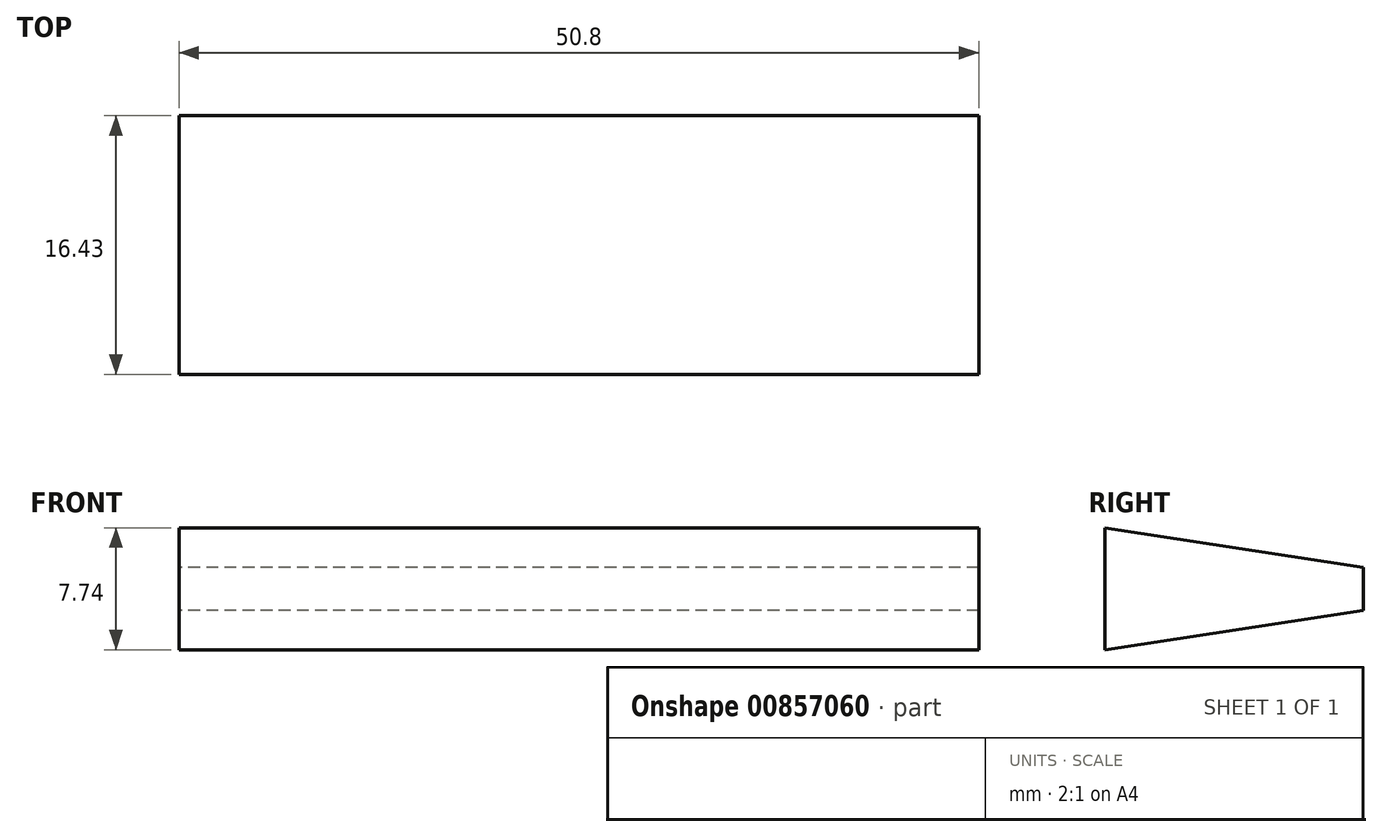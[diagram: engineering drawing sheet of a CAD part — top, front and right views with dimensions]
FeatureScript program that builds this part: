
annotation { "Feature Type Name" : "Feature", "Feature Type Description" : "" }
export const myFeature = defineFeature(function(context is Context, id is Id, definition is map)
    precondition{}
    {
        {
            var Q0;
            Q0=qCreatedBy(makeId("Right.planeOp"),FACE);
            var sketch = newSketch(context, id + "F0", { "sketchPlane" : qUnion([Q0])});
            skLineSegment(sketch, "E0", {"start": v(0, 48.82) * mm, "end": v(0, -48.82) * mm});
            skLineSegment(sketch, "E1", {"start": v(274.08, 7.08) * mm, "end": v(274.08, -7.08) * mm});
            skCircle(sketch, "E2", {"center": v(311.35, 0) * mm, "radius": 1.39 * mm});
            skLineSegment(sketch, "E3", {"start": v(0, 48.82) * mm, "end": v(311.56, 1.37) * mm});
            skLineSegment(sketch, "E4", {"start": v(0, -48.82) * mm, "end": v(311.56, -1.37) * mm});
            skLineSegment(sketch, "E5", {"start": v(274.08, 3.87) * mm, "end": v(299.48, 0) * mm});
            skLineSegment(sketch, "E6", {"start": v(299.48, 0) * mm, "end": v(274.08, -3.87) * mm});
            skLineSegment(sketch, "E7", {"start": v(312.74, 0) * mm, "end": v(290.51, 0) * mm});
            skLineSegment(sketch, "E8", {"start": v(290.51, 1.37) * mm, "end": v(290.51, -1.37) * mm});
            skSolve(sketch);
        }
        {
            var Q0;
            {var subQ2=sQuery(id+"F0.wireOp",EDGE,"E5");var subQ5=sQuery(id+"F0.wireOp",EDGE,"E1");var subQ8=makeQuery(id+"F0.imprint","INTERSECT",VERTEX,{"derivedFrom":[subQ5,subQ2]});Q0=makeQuery(id+"F0.imprint","IMPRINT",FACE,{"disambiguationData":[TD([[makeQuery(id+"F0.imprint","IMPRINT",EDGE,{"disambiguationData":[TD([[subQ8,-1.0]])],"derivedFrom":subQ5}),1.0]])]});}
            extrude(context, id + "F1", {"entities" : qUnion([Q0]), "depth" : 50.8 * mm, "offsetDistance" : 25.4 * mm, "symmetric" : true});
        }
    });
